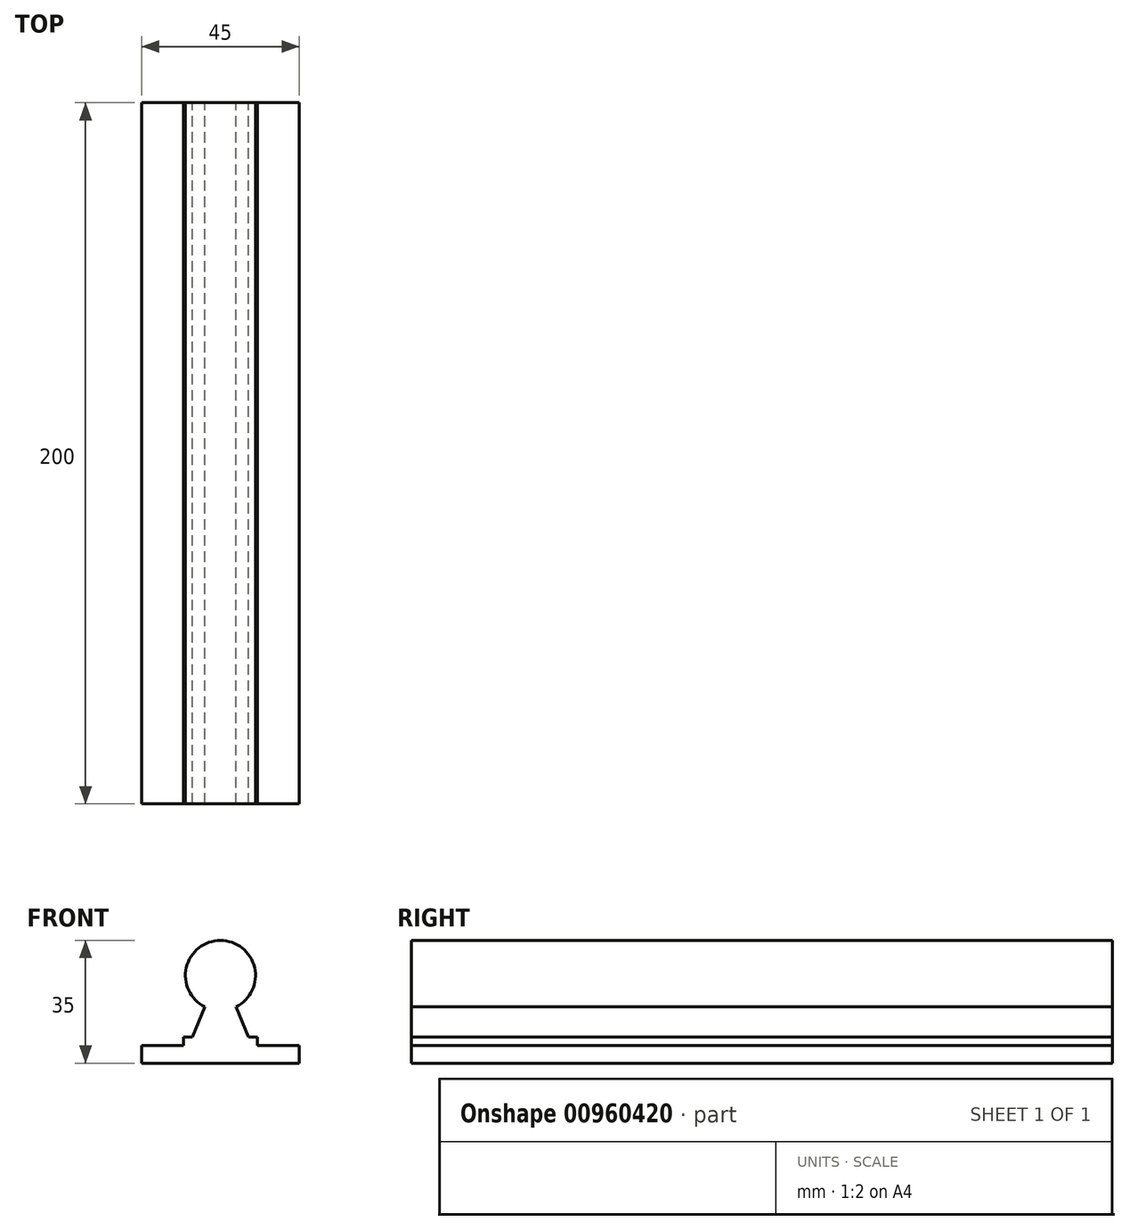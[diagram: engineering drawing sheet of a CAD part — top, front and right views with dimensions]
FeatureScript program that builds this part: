
annotation { "Feature Type Name" : "Feature", "Feature Type Description" : "" }
export const myFeature = defineFeature(function(context is Context, id is Id, definition is map)
    precondition{}
    {
        {
            var Q0;
            Q0=qCreatedBy(makeId("Front.planeOp"),FACE);
            var sketch = newSketch(context, id + "F0", { "sketchPlane" : qUnion([Q0])});
            skCircle(sketch, "E0", {"center": v(0, 0) * mm, "radius": 10 * mm});
            skLineSegment(sketch, "E1", {"start": v(-22.5, -25) * mm, "end": v(22.5, -25) * mm});
            skPoint(sketch, "E2", {"position": v(0, -25) * mm});
            skLineSegment(sketch, "E3", {"start": v(-22.5, -25) * mm, "end": v(-22.5, -20) * mm});
            skLineSegment(sketch, "E4", {"start": v(-22.5, -20) * mm, "end": v(-10.5, -20) * mm});
            skLineSegment(sketch, "E5", {"start": v(-10.5, -20) * mm, "end": v(-10.5, -17.5) * mm});
            skLineSegment(sketch, "E6", {"start": v(-10.5, -17.5) * mm, "end": v(-8, -17.5) * mm});
            skLineSegment(sketch, "E7", {"start": v(-8, -17.5) * mm, "end": v(-4.5, -8.93) * mm});
            skLineSegment(sketch, "E8", {"start": v(0, -29.05) * mm, "end": v(0, 13.28) * mm, "construction": true});
            skLineSegment(sketch, "E9.MirrorCS", {"start": v(8, -17.5) * mm, "end": v(4.5, -8.93) * mm});
            skLineSegment(sketch, "E10.MirrorCS", {"start": v(10.5, -17.5) * mm, "end": v(8, -17.5) * mm});
            skLineSegment(sketch, "E11.MirrorCS", {"start": v(10.5, -20) * mm, "end": v(10.5, -17.5) * mm});
            skLineSegment(sketch, "E12.MirrorCS", {"start": v(22.5, -20) * mm, "end": v(10.5, -20) * mm});
            skLineSegment(sketch, "E13.MirrorCS", {"start": v(22.5, -25) * mm, "end": v(22.5, -20) * mm});
            skSolve(sketch);
        }
        {
            var Q0;
            Q0=qSketchRegion(id+"F0",true);
            extrude(context, id + "F1", {"entities" : qUnion([Q0]), "depth" : 200 * mm, "offsetDistance" : 25 * mm});
        }
    });
